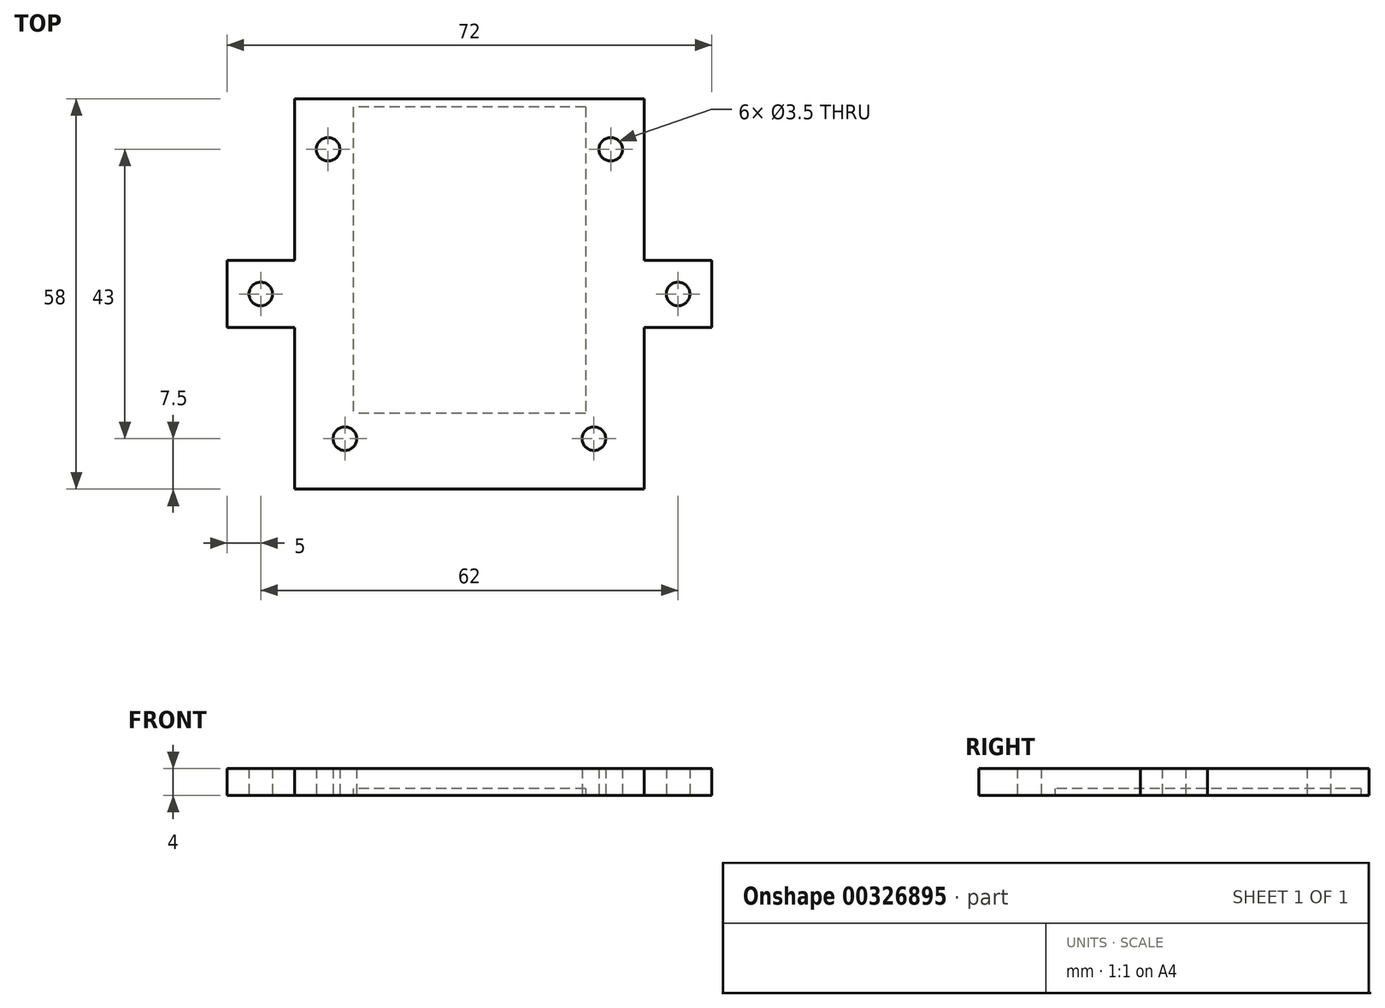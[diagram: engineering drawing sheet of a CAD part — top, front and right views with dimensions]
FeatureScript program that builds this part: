
annotation { "Feature Type Name" : "Feature", "Feature Type Description" : "" }
export const myFeature = defineFeature(function(context is Context, id is Id, definition is map)
    precondition{}
    {
        {
            var Q0;
            Q0=qCreatedBy(makeId("Top.planeOp"),FACE);
            var sketch = newSketch(context, id + "F0", { "sketchPlane" : qUnion([Q0])});
            skLineSegment(sketch, "E0.bottom", {"start": v(26, 29) * mm, "end": v(-26, 29) * mm});
            skLineSegment(sketch, "E0.top", {"start": v(26, -29) * mm, "end": v(-26, -29) * mm});
            skLineSegment(sketch, "E0.left", {"start": v(26, 29) * mm, "end": v(26, 5) * mm});
            skLineSegment(sketch, "E0.right", {"start": v(-26, 29) * mm, "end": v(-26, 5) * mm});
            skPoint(sketch, "E0.middle", {"position": v(0, 0) * mm});
            skLineSegment(sketch, "E1.bottom", {"start": v(26, 5) * mm, "end": v(36, 5) * mm});
            skLineSegment(sketch, "E1.top", {"start": v(26, -5) * mm, "end": v(36, -5) * mm});
            skLineSegment(sketch, "E1.right", {"start": v(36, 5) * mm, "end": v(36, -5) * mm});
            skPoint(sketch, "E1.middle", {"position": v(31, 0) * mm});
            skLineSegment(sketch, "E2.bottom", {"start": v(-26, 5) * mm, "end": v(-36, 5) * mm});
            skLineSegment(sketch, "E2.top", {"start": v(-26, -5) * mm, "end": v(-36, -5) * mm});
            skLineSegment(sketch, "E2.right", {"start": v(-36, 5) * mm, "end": v(-36, -5) * mm});
            skPoint(sketch, "E2.middle", {"position": v(-31, 0) * mm});
            skLineSegment(sketch, "E3.trimOffspring", {"start": v(26, -5) * mm, "end": v(26, -29) * mm});
            skLineSegment(sketch, "E4.trimOffspring", {"start": v(-26, -5) * mm, "end": v(-26, -29) * mm});
            skSolve(sketch);
        }
        {
            var Q0;
            Q0=qSketchRegion(id+"F0",true);
            extrude(context, id + "F1", {"entities" : qUnion([Q0]), "depth" : 4 * mm});
        }
        {
            var Q0;
            Q0=qCreatedBy(makeId("Top.planeOp"),FACE);
            var sketch = newSketch(context, id + "F2", { "sketchPlane" : qUnion([Q0])});
            skLineSegment(sketch, "E5.bottom", {"start": v(17.25, 27.78) * mm, "end": v(-17.25, 27.78) * mm});
            skLineSegment(sketch, "E5.top", {"start": v(17.25, -17.72) * mm, "end": v(-17.25, -17.72) * mm});
            skLineSegment(sketch, "E5.left", {"start": v(17.25, 27.78) * mm, "end": v(17.25, -17.72) * mm});
            skLineSegment(sketch, "E5.right", {"start": v(-17.25, 27.78) * mm, "end": v(-17.25, -17.72) * mm});
            skPoint(sketch, "E5.middle", {"position": v(0, 5.03) * mm});
            skSolve(sketch);
        }
        {
            var Q0;
            Q0=qSketchRegion(id+"F2",true);
            extrude(context, id + "F3", {"entities" : qUnion([Q0]), "operationType" : NewBodyOperationType.REMOVE, "depth" : 1 * mm});
        }
        {
            var Q0;
            Q0=qCreatedBy(makeId("Top.planeOp"),FACE);
            var sketch = newSketch(context, id + "F4", { "sketchPlane" : qUnion([Q0])});
            skPoint(sketch, "E6.middle", {"position": v(18.5, -21.5) * mm});
            skPoint(sketch, "E7.middle", {"position": v(-18.5, -21.5) * mm});
            skCircle(sketch, "E8", {"center": v(-18.5, -21.5) * mm, "radius": 1.75 * mm});
            skCircle(sketch, "E9", {"center": v(18.5, -21.5) * mm, "radius": 1.75 * mm});
            skPoint(sketch, "E10.middle", {"position": v(-21, 21.5) * mm});
            skCircle(sketch, "E11", {"center": v(-21, 21.5) * mm, "radius": 1.75 * mm});
            skPoint(sketch, "E12.middle", {"position": v(21, 21.5) * mm});
            skCircle(sketch, "E13", {"center": v(21, 21.5) * mm, "radius": 1.75 * mm});
            skPoint(sketch, "E14.middle", {"position": v(31, 0) * mm});
            skPoint(sketch, "E15.middle", {"position": v(-31, 0) * mm});
            skCircle(sketch, "E16", {"center": v(-31, 0) * mm, "radius": 1.75 * mm});
            skCircle(sketch, "E17", {"center": v(31, 0) * mm, "radius": 1.75 * mm});
            skSolve(sketch);
        }
        {
            var Q0;
            Q0 = qSketchRegion(id + "F4", true);
            extrude(context, id + "F5", {"entities" : qUnion([Q0]), "operationType" : NewBodyOperationType.REMOVE, "depth" : 25 * mm});
        }
    });
